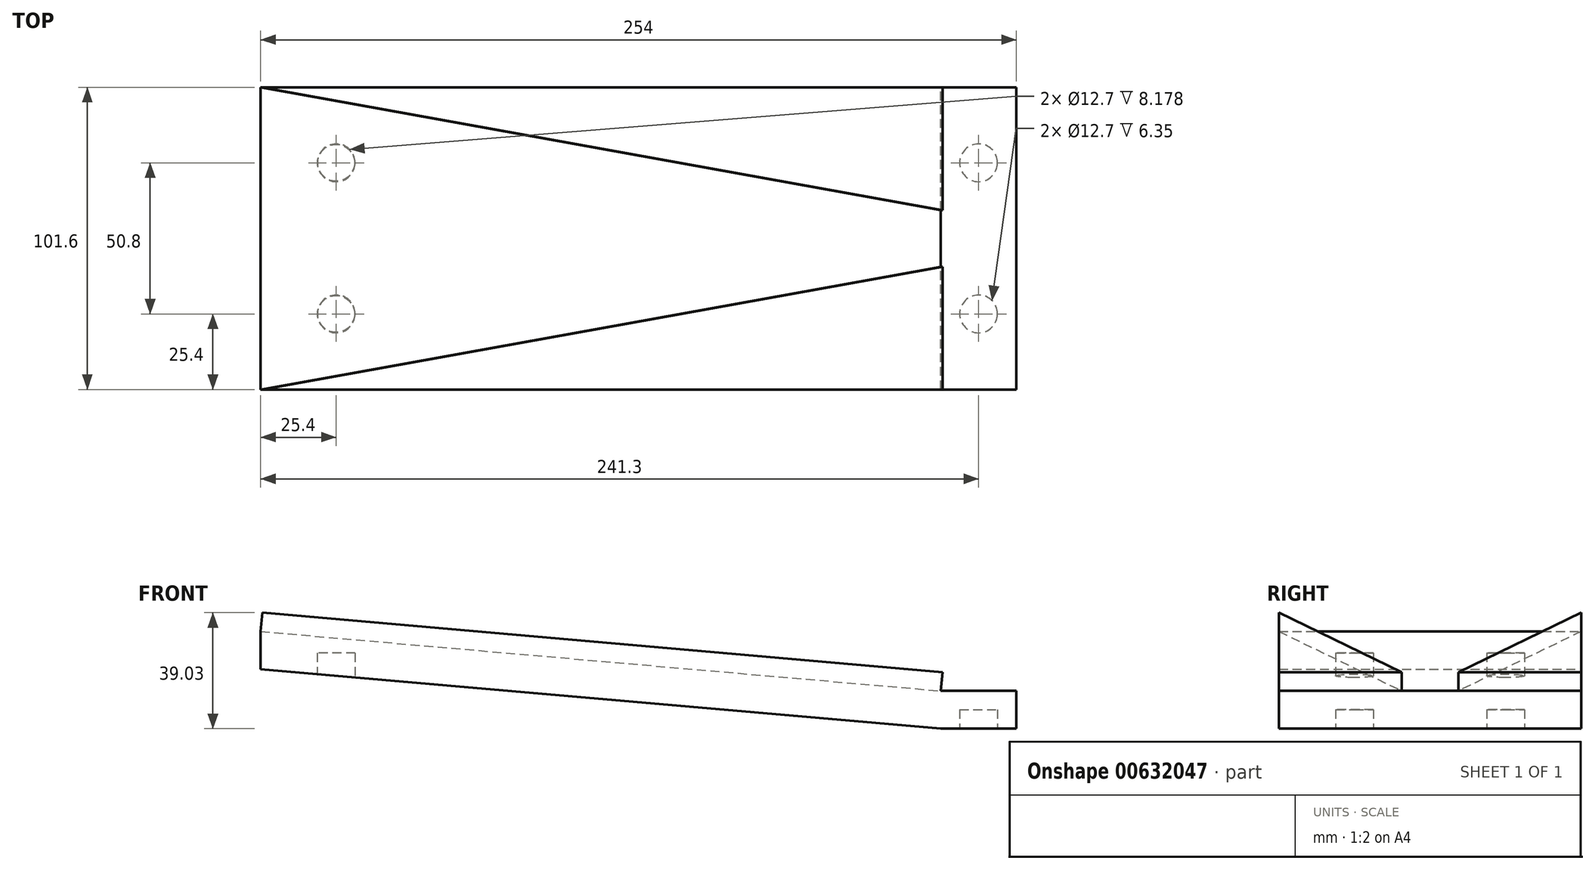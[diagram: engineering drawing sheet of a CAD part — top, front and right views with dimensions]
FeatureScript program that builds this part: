
annotation { "Feature Type Name" : "Feature", "Feature Type Description" : "" }
export const myFeature = defineFeature(function(context is Context, id is Id, definition is map)
    precondition{}
    {
        {
            var Q0;
            Q0=qCreatedBy(makeId("Front.planeOp"),FACE);
            var sketch = newSketch(context, id + "F0", { "sketchPlane" : qUnion([Q0])});
            skLineSegment(sketch, "E0", {"start": v(0, 0) * mm, "end": v(-25.4, 0) * mm});
            skLineSegment(sketch, "E1", {"start": v(-25.4, 0) * mm, "end": v(-254, 20) * mm});
            skLineSegment(sketch, "E2", {"start": v(-254, 20) * mm, "end": v(-254, 32.7) * mm});
            skLineSegment(sketch, "E3", {"start": v(-254, 32.7) * mm, "end": v(-25.4, 12.7) * mm});
            skLineSegment(sketch, "E4", {"start": v(-25.4, 12.7) * mm, "end": v(0, 12.7) * mm});
            skLineSegment(sketch, "E5", {"start": v(0, 12.7) * mm, "end": v(0, 0) * mm});
            skSolve(sketch);
        }
        {
            var Q0;
            Q0 = qSketchRegion(id + "F0", true);
            extrude(context, id + "F1", {"entities" : qUnion([Q0]), "depth" : 101.6 * mm, "offsetDistance" : 25.4 * mm});
        }
        {
            var Q0;
            Q0=makeQuery(id+"F1.opExtrude","SWEPT_FACE",FACE,{"disambiguationData":[OSD([sQuery(id+"F0.wireOp",EDGE,"E3")])]});
            var sketch = newSketch(context, id + "F2", { "sketchPlane" : qUnion([Q0])});
            skLineSegment(sketch, "E6", {"start": v(-255.88, 0) * mm, "end": v(-26.41, -41.28) * mm});
            skLineSegment(sketch, "E7", {"start": v(-26.41, -41.28) * mm, "end": v(-26.41, 0) * mm});
            skLineSegment(sketch, "E8", {"start": v(-26.41, 0) * mm, "end": v(-255.88, 0) * mm});
            skLineSegment(sketch, "E9", {"start": v(-255.88, -101.6) * mm, "end": v(-26.41, -60.32) * mm});
            skLineSegment(sketch, "E10", {"start": v(-26.41, -60.33) * mm, "end": v(-26.41, -101.6) * mm});
            skLineSegment(sketch, "E11", {"start": v(-26.41, -101.6) * mm, "end": v(-255.88, -101.6) * mm});
            skSolve(sketch);
        }
        {
            var Q0;
            Q0 = qSketchRegion(id + "F2", true);
            extrude(context, id + "F3", {"entities" : qUnion([Q0]), "operationType" : NewBodyOperationType.ADD, "depth" : 6.35 * mm, "offsetDistance" : 25.4 * mm});
        }
        {
            var Q0;
            Q0=qCreatedBy(makeId("Top.planeOp"),FACE);
            var sketch = newSketch(context, id + "F4", { "sketchPlane" : qUnion([Q0])});
            skCircle(sketch, "E12", {"center": v(-228.6, -25.4) * mm, "radius": 6.35 * mm});
            skCircle(sketch, "E13", {"center": v(-228.6, -76.2) * mm, "radius": 6.35 * mm});
            skSolve(sketch);
        }
        {
            var Q0;
            Q0 = qSketchRegion(id + "F4", true);
            extrude(context, id + "F5", {"entities" : qUnion([Q0]), "operationType" : NewBodyOperationType.REMOVE, "depth" : 25.4 * mm, "offsetDistance" : 25.4 * mm});
        }
        {
            var Q0;
            Q0=makeQuery(id+"F1.opExtrude","SWEPT_FACE",FACE,{"disambiguationData":[OSD([sQuery(id+"F0.wireOp",EDGE,"E0")])]});
            var sketch = newSketch(context, id + "F6", { "sketchPlane" : qUnion([Q0])});
            skCircle(sketch, "E14", {"center": v(-12.7, 25.4) * mm, "radius": 6.35 * mm});
            skPoint(sketch, "E14.centerSnap0", {"position": v(-12.7, 0) * mm});
            skCircle(sketch, "E15", {"center": v(-12.7, 76.2) * mm, "radius": 6.35 * mm});
            skPoint(sketch, "E15.centerSnap0", {"position": v(-12.7, 101.6) * mm});
            skSolve(sketch);
        }
        {
            var Q0;
            Q0 = qSketchRegion(id + "F6", true);
            extrude(context, id + "F7", {"entities" : qUnion([Q0]), "operationType" : NewBodyOperationType.REMOVE, "oppositeDirection" : true, "depth" : 6.35 * mm, "offsetDistance" : 25.4 * mm});
        }
    });
